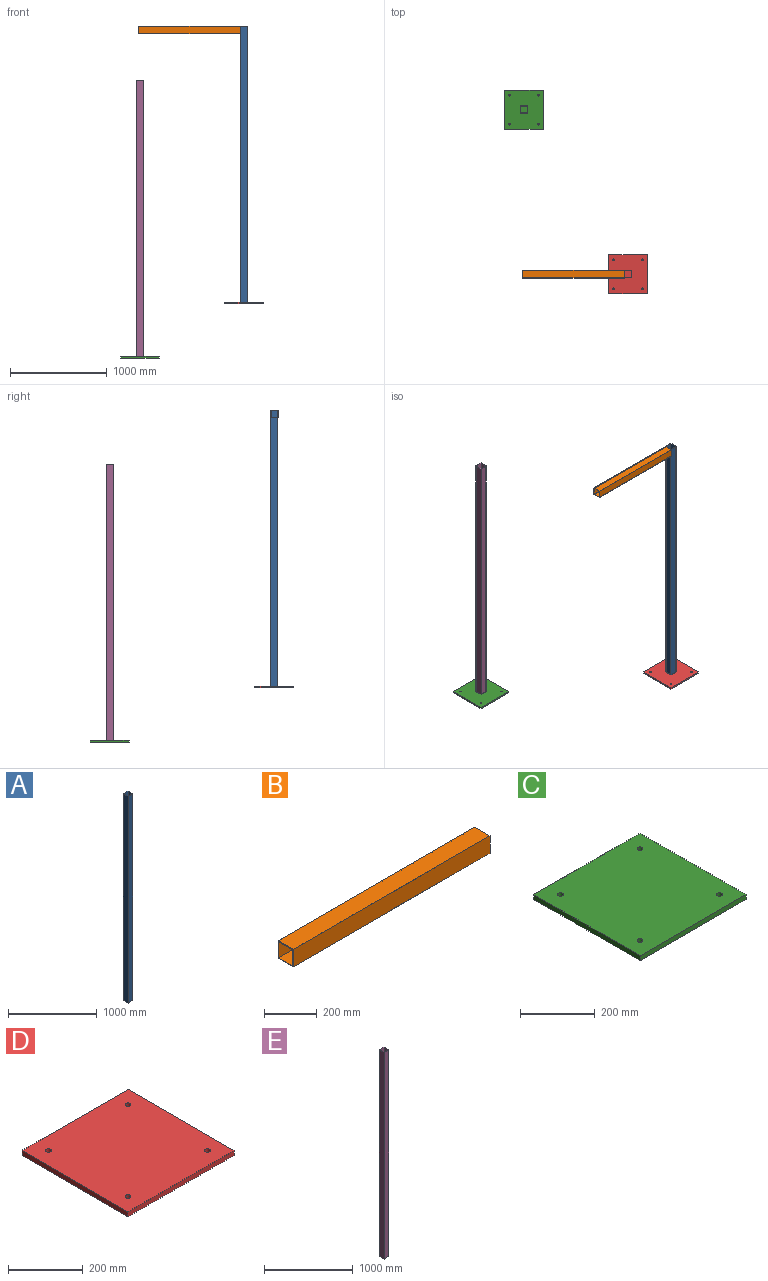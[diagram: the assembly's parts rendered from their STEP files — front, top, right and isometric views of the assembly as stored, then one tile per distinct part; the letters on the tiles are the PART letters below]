
ASSEMBLY  parts=5 mates=4
PART A: 10 faces, bbox 75x75x2857 mm
  f0: plane 2857x75mm, normal (0,1,0), area 214275mm2, adj f1,f7,f8,f9
  f1: plane 2857x75mm, normal (-1,0,0), area 214275mm2, adj f0,f2,f8,f9
  f2: plane 2857x75mm, normal (0,-1,0), area 214275mm2, adj f1,f7,f8,f9
  f3: plane 2857x69mm, normal (0,-1,0), area 197133mm2, adj f4,f6,f8,f9
  f4: plane 2857x69mm, normal (-1,0,0), area 197133mm2, adj f3,f5,f8,f9
  f5: plane 2857x69mm, normal (0,1,0), area 197133mm2, adj f4,f6,f8,f9
  f6: plane 2857x69mm, normal (1,0,0), area 197133mm2, adj f3,f5,f8,f9
  f7: plane 2857x75mm, normal (1,0,0), area 214275mm2, adj f0,f2,f8,f9
  f8: plane 75x75mm, normal (0,0,1), area 864mm2, adj f0,f1,f2,f3,f4,f5,f6,f7
  f9: plane 75x75mm, normal (0,0,-1), area 864mm2, adj f0,f1,f2,f3,f4,f5,f6,f7
PART B: 10 faces, bbox 1054x81x81 mm
  f0: plane 1054x75mm, normal (0,0,1), area 79050mm2, adj f1,f7,f8,f9
  f1: plane 1054x75mm, normal (0,1,0), area 79050mm2, adj f0,f2,f8,f9
  f2: plane 1054x75mm, normal (0,0,-1), area 79050mm2, adj f1,f7,f8,f9
  f3: plane 1054x81mm, normal (0,0,-1), area 85374mm2, adj f4,f6,f8,f9
  f4: plane 1054x81mm, normal (0,1,0), area 85374mm2, adj f3,f5,f8,f9
  f5: plane 1054x81mm, normal (0,0,1), area 85374mm2, adj f4,f6,f8,f9
  f6: plane 1054x81mm, normal (0,-1,0), area 85374mm2, adj f3,f5,f8,f9
  f7: plane 1054x75mm, normal (0,-1,0), area 79050mm2, adj f0,f2,f8,f9
  f8: plane 81x81mm, normal (1,0,0), area 936mm2, adj f0,f1,f2,f3,f4,f5,f6,f7
  f9: plane 81x81mm, normal (-1,0,0), area 936mm2, adj f0,f1,f2,f3,f4,f5,f6,f7
PART C: 10 faces, bbox 400x400x16 mm
  f0: plane 400x16mm, normal (0,-1,0), area 6400mm2, adj f1,f7,f8,f9
  f1: plane 400x16mm, normal (1,0,0), area 6400mm2, adj f0,f2,f8,f9
  f2: plane 400x16mm, normal (0,1,0), area 6400mm2, adj f1,f7,f8,f9
  f3: cylinder r=8mm len=16mm, axis (0,0,-1), area 804.2mm2, adj f8,f9
  f4: cylinder r=8mm len=16mm, axis (0,0,-1), area 804.2mm2, adj f8,f9
  f5: cylinder r=8mm len=16mm, axis (0,0,-1), area 804.2mm2, adj f8,f9
  f6: cylinder r=8mm len=16mm, axis (0,0,-1), area 804.2mm2, adj f8,f9
  f7: plane 400x16mm, normal (-1,0,0), area 6400mm2, adj f0,f2,f8,f9
  f8: plane 400x400mm, normal (0,0,1), area 159195.8mm2, adj f0,f1,f2,f3,f4,f5,f6,f7
  f9: plane 400x400mm, normal (0,0,-1), area 159195.8mm2, adj f0,f1,f2,f3,f4,f5,f6,f7
PART D: 10 faces, bbox 400x400x16 mm
  f0: plane 400x16mm, normal (0,-1,0), area 6400mm2, adj f1,f7,f8,f9
  f1: plane 400x16mm, normal (1,0,0), area 6400mm2, adj f0,f2,f8,f9
  f2: plane 400x16mm, normal (0,1,0), area 6400mm2, adj f1,f7,f8,f9
  f3: cylinder r=8mm len=16mm, axis (0,0,-1), area 804.2mm2, adj f8,f9
  f4: cylinder r=8mm len=16mm, axis (0,0,-1), area 804.2mm2, adj f8,f9
  f5: cylinder r=8mm len=16mm, axis (0,0,-1), area 804.2mm2, adj f8,f9
  f6: cylinder r=8mm len=16mm, axis (0,0,-1), area 804.2mm2, adj f8,f9
  f7: plane 400x16mm, normal (-1,0,0), area 6400mm2, adj f0,f2,f8,f9
  f8: plane 400x400mm, normal (0,0,1), area 159195.8mm2, adj f0,f1,f2,f3,f4,f5,f6,f7
  f9: plane 400x400mm, normal (0,0,-1), area 159195.8mm2, adj f0,f1,f2,f3,f4,f5,f6,f7
PART E: 10 faces, bbox 75x75x2857 mm
  f0: plane 2857x75mm, normal (0,1,0), area 214275mm2, adj f1,f7,f8,f9
  f1: plane 2857x75mm, normal (-1,0,0), area 214275mm2, adj f0,f2,f8,f9
  f2: plane 2857x75mm, normal (0,-1,0), area 214275mm2, adj f1,f7,f8,f9
  f3: plane 2857x69mm, normal (0,-1,0), area 197133mm2, adj f4,f6,f8,f9
  f4: plane 2857x69mm, normal (-1,0,0), area 197133mm2, adj f3,f5,f8,f9
  f5: plane 2857x69mm, normal (0,1,0), area 197133mm2, adj f4,f6,f8,f9
  f6: plane 2857x69mm, normal (1,0,0), area 197133mm2, adj f3,f5,f8,f9
  f7: plane 2857x75mm, normal (1,0,0), area 214275mm2, adj f0,f2,f8,f9
  f8: plane 75x75mm, normal (0,0,1), area 864mm2, adj f0,f1,f2,f3,f4,f5,f6,f7
  f9: plane 75x75mm, normal (0,0,-1), area 864mm2, adj f0,f1,f2,f3,f4,f5,f6,f7
PLACE A t=(806.07,-1334.19,-208.12)mm
PLACE B t=(-345.11,-1298.04,2732.49)mm
PLACE C t=(-503.63,-755.74,-784.18)mm
PLACE D t=(573.66,-1728.64,-224.12)mm
PLACE E t=(-271.23,-67.29,-2731.18)mm
MATE fastened D.f8 <-> A.f9  axis (0,0,1) through (746.39,-1330.52,-208.12)mm
MATE fastened C.f8 <-> E.f9  axis (0,0,1) through (-330.9,370.38,-768.18)mm
MATE planar B.f5 <-> A.f8  axis (0,0,1) through (708.89,-1335.36,2648.88)mm
MATE planar A.f1 <-> B.f8  axis (-1,0,0) through (708.89,-1330.52,1220.38)mm
